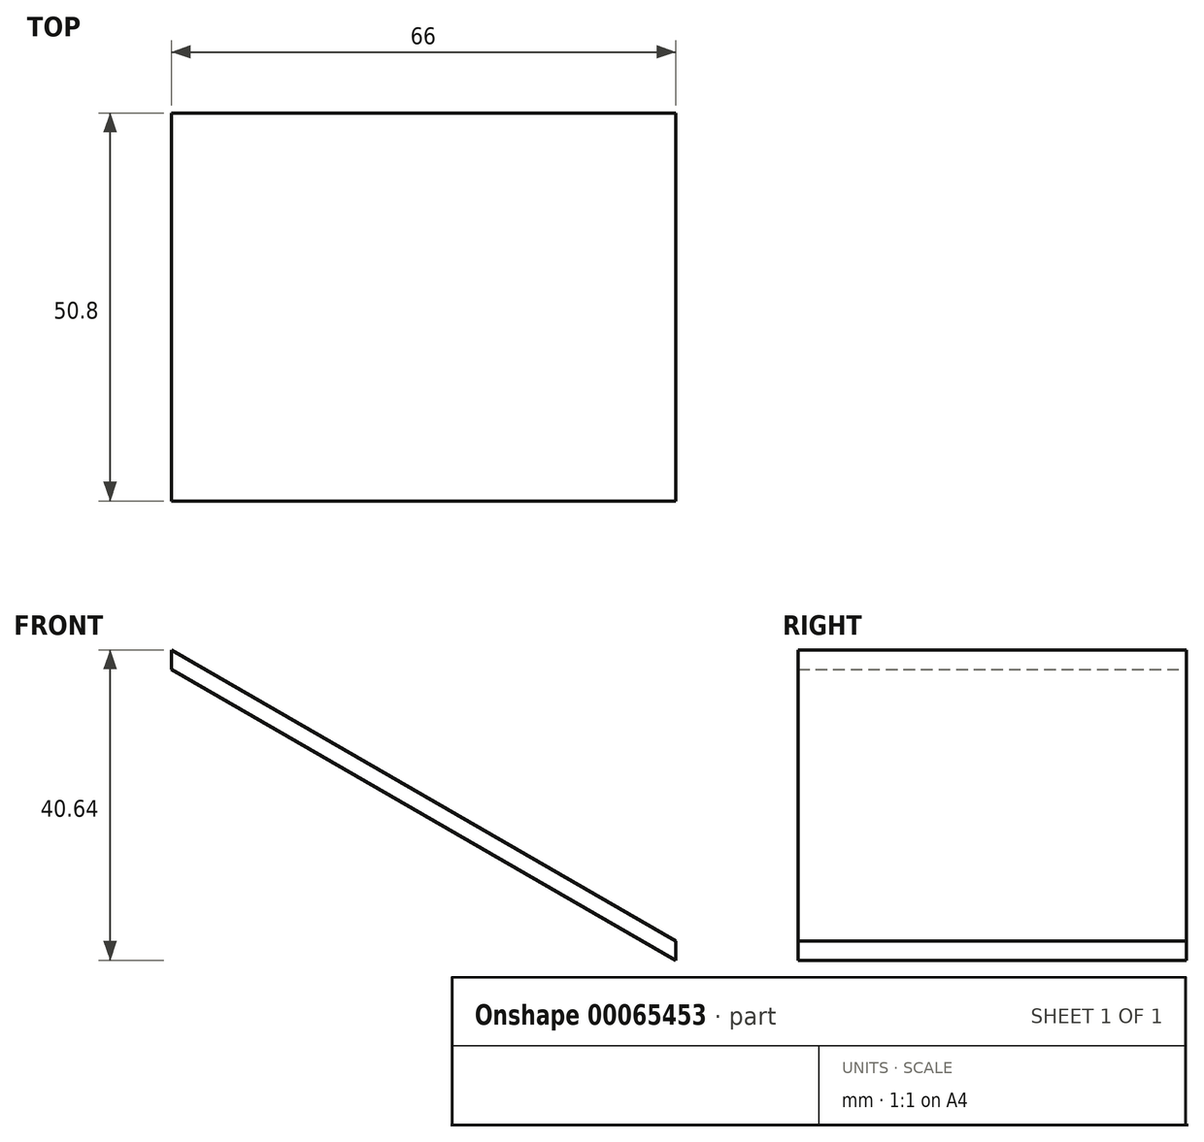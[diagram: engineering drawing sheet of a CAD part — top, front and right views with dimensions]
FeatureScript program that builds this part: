
annotation { "Feature Type Name" : "Feature", "Feature Type Description" : "" }
export const myFeature = defineFeature(function(context is Context, id is Id, definition is map)
    precondition{}
    {
        {
            var Q0;
            Q0=qCreatedBy(makeId("Front.planeOp"),FACE);
            var sketch = newSketch(context, id + "F0", { "sketchPlane" : qUnion([Q0])});
            skLineSegment(sketch, "E0", {"start": v(-47.29, 0) * mm, "end": v(18.7, 0) * mm});
            skLineSegment(sketch, "E1", {"start": v(18.7, 0) * mm, "end": v(18.7, -38.1) * mm});
            skLineSegment(sketch, "E2", {"start": v(18.7, -38.1) * mm, "end": v(-47.29, 0) * mm});
            skLineSegment(sketch, "E3", {"start": v(-47.29, 0) * mm, "end": v(-47.29, -2.54) * mm});
            skLineSegment(sketch, "E4", {"start": v(18.7, -38.1) * mm, "end": v(18.7, -40.64) * mm});
            skLineSegment(sketch, "E5", {"start": v(18.7, -40.64) * mm, "end": v(-47.29, -2.54) * mm});
            skSolve(sketch);
        }
        {
            var Q0;
            Q0=makeQuery(id+"F0.imprint","IMPRINT",FACE,{"disambiguationData":[TD([[makeQuery(id+"F0.imprint","IMPRINT",EDGE,{"derivedFrom":sQuery(id+"F0.wireOp",EDGE,"E2")}),1.0]])]});
            extrude(context, id + "F1", {"entities" : qUnion([Q0]), "depth" : 50.8 * mm});
        }
    });
